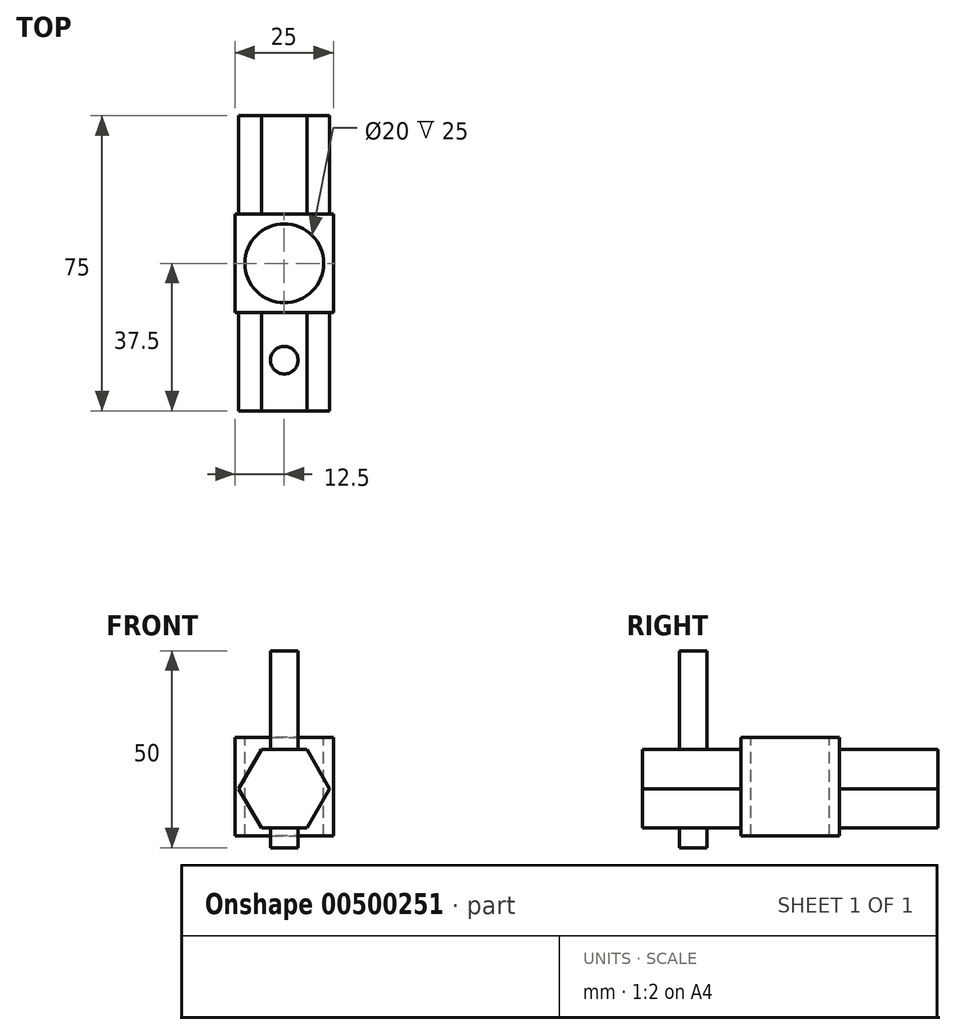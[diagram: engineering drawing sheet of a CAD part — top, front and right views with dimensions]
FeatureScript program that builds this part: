
annotation { "Feature Type Name" : "Feature", "Feature Type Description" : "" }
export const myFeature = defineFeature(function(context is Context, id is Id, definition is map)
    precondition{}
    {
        {
            var Q0;
            Q0=qCreatedBy(makeId("Top.planeOp"),FACE);
            var sketch = newSketch(context, id + "F0", { "sketchPlane" : qUnion([Q0])});
            skLineSegment(sketch, "E0.bottom", {"start": v(-12.5, 12.5) * mm, "end": v(12.5, 12.5) * mm});
            skLineSegment(sketch, "E0.top", {"start": v(-12.5, -12.5) * mm, "end": v(12.5, -12.5) * mm});
            skLineSegment(sketch, "E0.left", {"start": v(-12.5, 12.5) * mm, "end": v(-12.5, -12.5) * mm});
            skLineSegment(sketch, "E0.right", {"start": v(12.5, 12.5) * mm, "end": v(12.5, -12.5) * mm});
            skPoint(sketch, "E0.middle", {"position": v(0, 0) * mm});
            skSolve(sketch);
        }
        {
            var Q0;
            Q0=makeQuery(id+"F0.imprint","IMPRINT",FACE,{"disambiguationData":[TD([[makeQuery(id+"F0.imprint","IMPRINT",EDGE,{"derivedFrom":sQuery(id+"F0.wireOp",EDGE,"E0.bottom")}),-1.0]])]});
            extrude(context, id + "F1", {"entities" : qUnion([Q0]), "depth" : 25 * mm});
        }
        {
            var Q0;
            Q0=makeQuery(id+"F1.opExtrude","CAP_FACE",FACE,{"disambiguationData":[OSD([sQuery(id+"F0.wireOp",EDGE,"E0.bottom"),sQuery(id+"F0.wireOp",EDGE,"E0.top"),sQuery(id+"F0.wireOp",EDGE,"E0.left"),sQuery(id+"F0.wireOp",EDGE,"E0.right")])],"isStart":false});
            var sketch = newSketch(context, id + "F2", { "sketchPlane" : qUnion([Q0])});
            skCircle(sketch, "E1", {"center": v(0, 0) * mm, "radius": 10 * mm});
            skSolve(sketch);
        }
        {
            var Q0;
            Q0=makeQuery(id+"F2.imprint","IMPRINT",FACE,{"disambiguationData":[TD([[makeQuery(id+"F2.imprint","IMPRINT",EDGE,{"derivedFrom":sQuery(id+"F2.wireOp",EDGE,"E1")}),1.0]])]});
            extrude(context, id + "F3", {"entities" : qUnion([Q0]), "operationType" : NewBodyOperationType.REMOVE, "endBound" : BoundingType.THROUGH_ALL, "oppositeDirection" : true, "depth" : 25 * mm});
        }
        {
            var Q0;
            Q0=makeQuery(id+"F1.opExtrude","SWEPT_FACE",FACE,{"disambiguationData":[OSD([sQuery(id+"F0.wireOp",EDGE,"E0.bottom")])]});
            var sketch = newSketch(context, id + "F4", { "sketchPlane" : qUnion([Q0])});
            skCircle(sketch, "E2.cCircle", {"center": v(0, 12) * mm, "radius": 10 * mm, "construction": true});
            skLineSegment(sketch, "E2.0", {"start": v(-5.77, 2) * mm, "end": v(-11.55, 12) * mm});
            skLineSegment(sketch, "E2.1", {"start": v(-11.55, 12) * mm, "end": v(-5.77, 22) * mm});
            skLineSegment(sketch, "E2.2", {"start": v(-5.77, 22) * mm, "end": v(5.77, 22) * mm});
            skLineSegment(sketch, "E2.3", {"start": v(5.77, 22) * mm, "end": v(11.55, 12) * mm});
            skLineSegment(sketch, "E2.4", {"start": v(11.55, 12) * mm, "end": v(5.77, 2) * mm});
            skLineSegment(sketch, "E2.5", {"start": v(5.77, 2) * mm, "end": v(-5.77, 2) * mm});
            skPoint(sketch, "E2.0.midPoint", {"position": v(-8.66, 7) * mm});
            skSolve(sketch);
        }
        {
            var Q0;
            Q0=makeQuery(id+"F4.imprint","IMPRINT",FACE,{"disambiguationData":[TD([[makeQuery(id+"F4.imprint","IMPRINT",EDGE,{"derivedFrom":sQuery(id+"F4.wireOp",EDGE,"E2.0")}),-1.0]])]});
            extrude(context, id + "F5", {"entities" : qUnion([Q0]), "operationType" : NewBodyOperationType.ADD, "depth" : 25 * mm});
        }
        {
            var Q0;
            Q0=makeQuery(id+"F1.opExtrude","SWEPT_FACE",FACE,{"disambiguationData":[OSD([sQuery(id+"F0.wireOp",EDGE,"E0.top")])]});
            var sketch = newSketch(context, id + "F6", { "sketchPlane" : qUnion([Q0])});
            skCircle(sketch, "E3.cCircle", {"center": v(0, 12) * mm, "radius": 10 * mm, "construction": true});
            skLineSegment(sketch, "E3.0", {"start": v(11.55, 12) * mm, "end": v(5.77, 2) * mm});
            skLineSegment(sketch, "E3.1", {"start": v(5.77, 2) * mm, "end": v(-5.77, 2) * mm});
            skLineSegment(sketch, "E3.2", {"start": v(-5.77, 2) * mm, "end": v(-11.55, 12) * mm});
            skLineSegment(sketch, "E3.3", {"start": v(-11.55, 12) * mm, "end": v(-5.77, 22) * mm});
            skLineSegment(sketch, "E3.4", {"start": v(-5.77, 22) * mm, "end": v(5.77, 22) * mm});
            skLineSegment(sketch, "E3.5", {"start": v(5.77, 22) * mm, "end": v(11.55, 12) * mm});
            skPoint(sketch, "E3.0.midPoint", {"position": v(8.66, 7) * mm});
            skSolve(sketch);
        }
        {
            var Q0;
            Q0=makeQuery(id+"F6.imprint","IMPRINT",FACE,{"disambiguationData":[TD([[makeQuery(id+"F6.imprint","IMPRINT",EDGE,{"derivedFrom":sQuery(id+"F6.wireOp",EDGE,"E3.0")}),-1.0]])]});
            extrude(context, id + "F7", {"entities" : qUnion([Q0]), "depth" : 25 * mm});
        }
        {
            var Q0;
            Q0=makeQuery(id+"F7.opExtrude","SWEPT_FACE",FACE,{"disambiguationData":[OSD([sQuery(id+"F6.wireOp",EDGE,"E3.4")])]});
            var sketch = newSketch(context, id + "F8", { "sketchPlane" : qUnion([Q0])});
            skCircle(sketch, "E4", {"center": v(0, -24.6) * mm, "radius": 3.5 * mm});
            skSolve(sketch);
        }
        {
            var Q0;
            Q0=makeQuery(id+"F8.imprint","IMPRINT",FACE,{"disambiguationData":[TD([[makeQuery(id+"F8.imprint","IMPRINT",EDGE,{"derivedFrom":sQuery(id+"F8.wireOp",EDGE,"E4")}),1.0]])]});
            extrude(context, id + "F9", {"entities" : qUnion([Q0]), "operationType" : NewBodyOperationType.ADD, "depth" : 25 * mm, "hasSecondDirection" : true, "secondDirectionOppositeDirection" : true, "secondDirectionDepth" : 25 * mm});
        }
    });
